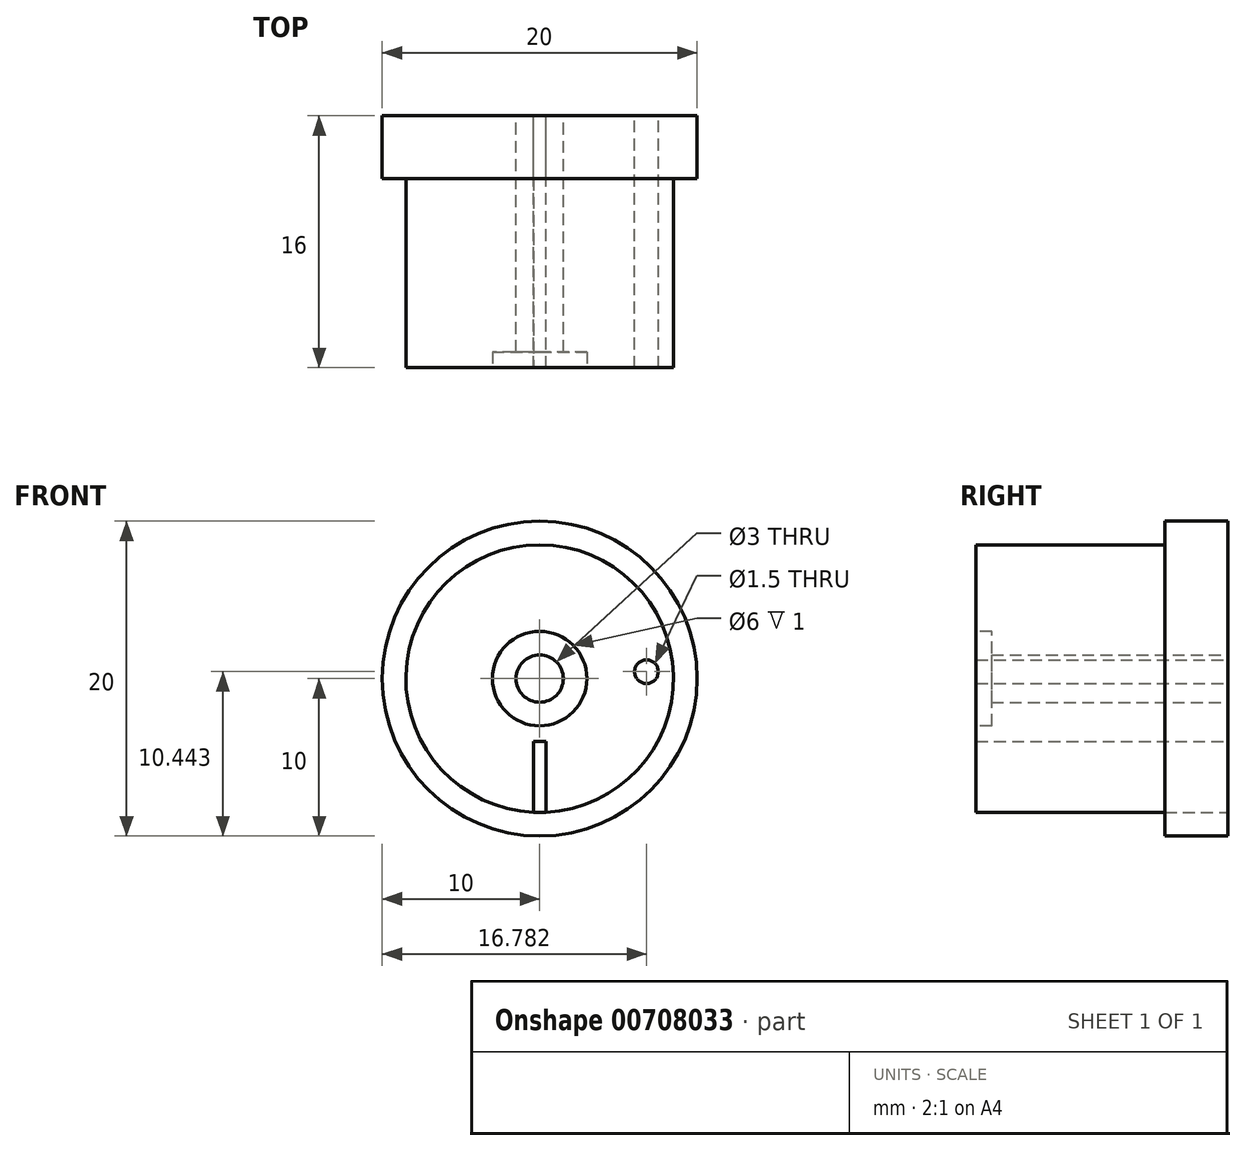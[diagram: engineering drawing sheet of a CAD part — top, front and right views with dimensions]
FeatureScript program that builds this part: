
annotation { "Feature Type Name" : "Feature", "Feature Type Description" : "" }
export const myFeature = defineFeature(function(context is Context, id is Id, definition is map)
    precondition{}
    {
        {
            var Q0;
            Q0=qCreatedBy(makeId("Front.planeOp"),FACE);
            var sketch = newSketch(context, id + "F0", { "sketchPlane" : qUnion([Q0])});
            skCircle(sketch, "E0", {"center": v(0, 0) * mm, "radius": 10 * mm});
            skSolve(sketch);
        }
        {
            var Q0;
            Q0 = qSketchRegion(id + "F0", true);
            extrude(context, id + "F1", {"entities" : qUnion([Q0]), "depth" : 4 * mm, "offsetDistance" : 25 * mm});
        }
        {
            var Q0;
            Q0=makeQuery(id+"F1.opExtrude","CAP_FACE",FACE,{"disambiguationData":[OSD([sQuery(id+"F0.wireOp",EDGE,"E0")])],"isStart":false});
            var sketch = newSketch(context, id + "F2", { "sketchPlane" : qUnion([Q0])});
            skCircle(sketch, "E1", {"center": v(0, 0) * mm, "radius": 8.5 * mm});
            skSolve(sketch);
        }
        {
            var Q0;
            Q0 = qSketchRegion(id + "F2", true);
            extrude(context, id + "F3", {"entities" : qUnion([Q0]), "operationType" : NewBodyOperationType.ADD, "depth" : 12 * mm, "offsetDistance" : 25 * mm});
        }
        {
            var Q0;
            Q0=makeQuery(id+"F1.opExtrude","CAP_FACE",FACE,{"disambiguationData":[OSD([sQuery(id+"F0.wireOp",EDGE,"E0")])],"isStart":true});
            var sketch = newSketch(context, id + "F4", { "sketchPlane" : qUnion([Q0])});
            skLineSegment(sketch, "E2.bottom", {"start": v(-0.4, -4) * mm, "end": v(0.4, -4) * mm});
            skLineSegment(sketch, "E2.top", {"start": v(-0.4, -8.5) * mm, "end": v(0.4, -8.5) * mm});
            skLineSegment(sketch, "E2.left", {"start": v(-0.4, -4) * mm, "end": v(-0.4, -8.5) * mm});
            skLineSegment(sketch, "E2.right", {"start": v(0.4, -4) * mm, "end": v(0.4, -8.5) * mm});
            skSolve(sketch);
        }
        {
            var Q0;
            Q0 = qSketchRegion(id + "F4", true);
            extrude(context, id + "F5", {"entities" : qUnion([Q0]), "operationType" : NewBodyOperationType.REMOVE, "endBound" : BoundingType.THROUGH_ALL, "oppositeDirection" : true, "depth" : 25 * mm, "offsetDistance" : 25 * mm});
        }
        {
            var Q0;
            Q0=makeQuery(id+"F1.opExtrude","CAP_FACE",FACE,{"disambiguationData":[OSD([sQuery(id+"F0.wireOp",EDGE,"E0")])],"isStart":true});
            var sketch = newSketch(context, id + "F6", { "sketchPlane" : qUnion([Q0])});
            skCircle(sketch, "E3", {"center": v(0, 0) * mm, "radius": 1.5 * mm});
            skSolve(sketch);
        }
        {
            var Q0;
            Q0 = qSketchRegion(id + "F6", true);
            extrude(context, id + "F7", {"entities" : qUnion([Q0]), "operationType" : NewBodyOperationType.REMOVE, "endBound" : BoundingType.THROUGH_ALL, "oppositeDirection" : true, "depth" : 25 * mm, "offsetDistance" : 25 * mm});
        }
        {
            var Q0;
            Q0=makeQuery(id+"F1.opExtrude","CAP_FACE",FACE,{"disambiguationData":[OSD([sQuery(id+"F0.wireOp",EDGE,"E0")])],"isStart":true});
            var sketch = newSketch(context, id + "F8", { "sketchPlane" : qUnion([Q0])});
            skCircle(sketch, "E4", {"center": v(-6.78, 0.44) * mm, "radius": 0.75 * mm});
            skSolve(sketch);
        }
        {
            var Q0;
            Q0 = qSketchRegion(id + "F8", true);
            extrude(context, id + "F9", {"entities" : qUnion([Q0]), "operationType" : NewBodyOperationType.REMOVE, "oppositeDirection" : true, "depth" : 25 * mm, "offsetDistance" : 25 * mm});
        }
        {
            var Q0;
            Q0=makeQuery(id+"F3.opExtrude","CAP_FACE",FACE,{"disambiguationData":[OSD([sQuery(id+"F2.wireOp",EDGE,"E1")])],"isStart":false});
            var sketch = newSketch(context, id + "F10", { "sketchPlane" : qUnion([Q0])});
            skCircle(sketch, "E5", {"center": v(0, 0) * mm, "radius": 3 * mm});
            skSolve(sketch);
        }
        {
            var Q0;
            Q0=makeQuery(id+"F10.imprint","IMPRINT",FACE,{"disambiguationData":[TD([[makeQuery(id+"F10.imprint","IMPRINT",EDGE,{"derivedFrom":sQuery(id+"F10.wireOp",EDGE,"E5")}),1.0]])]});
            extrude(context, id + "F11", {"entities" : qUnion([Q0]), "operationType" : NewBodyOperationType.REMOVE, "oppositeDirection" : true, "depth" : 1 * mm, "offsetDistance" : 25 * mm});
        }
    });
